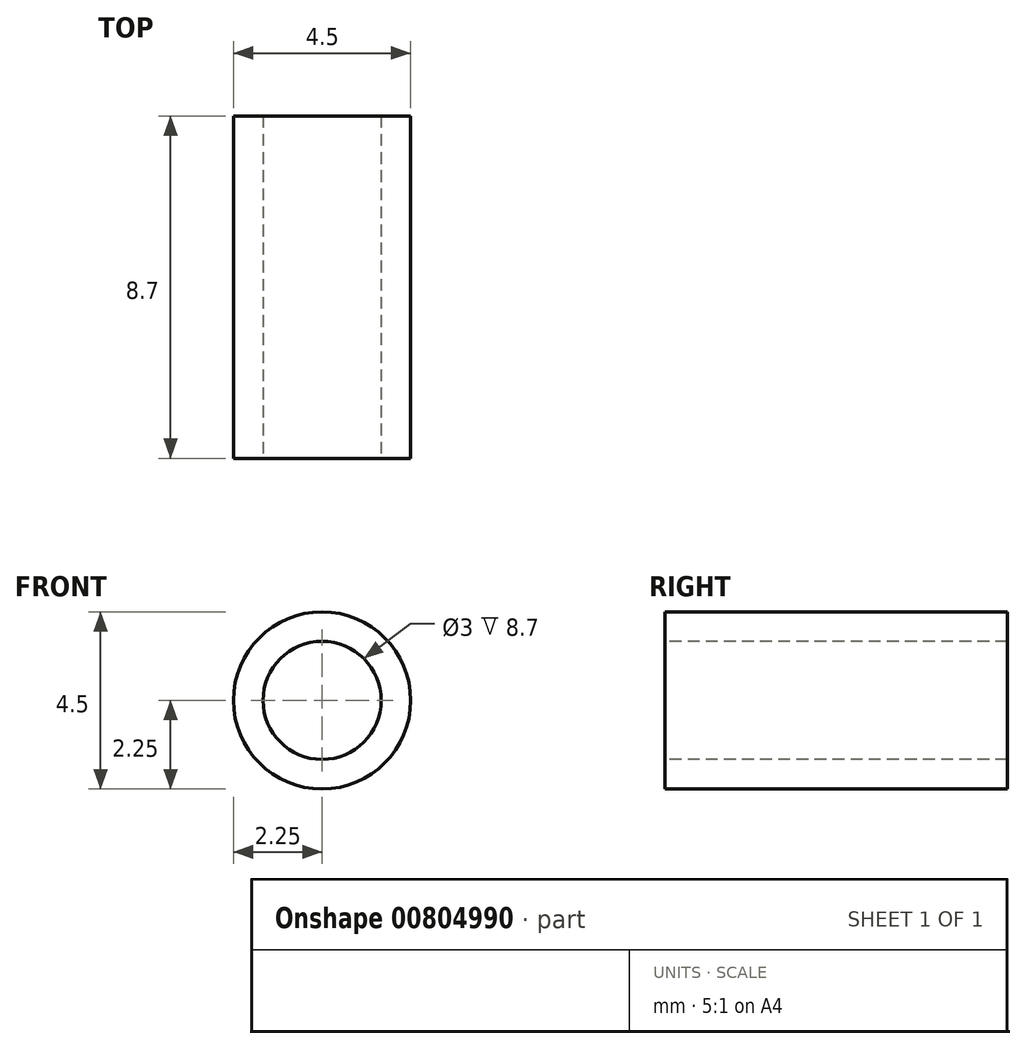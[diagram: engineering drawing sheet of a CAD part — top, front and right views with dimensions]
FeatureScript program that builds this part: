
annotation { "Feature Type Name" : "Feature", "Feature Type Description" : "" }
export const myFeature = defineFeature(function(context is Context, id is Id, definition is map)
    precondition{}
    {
        {
            var Q0;
            Q0=qCreatedBy(makeId("Right.planeOp"),FACE);
            var sketch = newSketch(context, id + "F0", { "sketchPlane" : qUnion([Q0])});
            skLineSegment(sketch, "E0.bottom", {"start": v(4.35, 1.5) * mm, "end": v(-4.35, 1.5) * mm});
            skLineSegment(sketch, "E0.top", {"start": v(4.35, 2.25) * mm, "end": v(-4.35, 2.25) * mm});
            skLineSegment(sketch, "E0.left", {"start": v(4.35, 1.5) * mm, "end": v(4.35, 2.25) * mm});
            skLineSegment(sketch, "E0.right", {"start": v(-4.35, 1.5) * mm, "end": v(-4.35, 2.25) * mm});
            skPoint(sketch, "E0.middle", {"position": v(0, 1.87) * mm});
            skLineSegment(sketch, "E1", {"start": v(-3.4, 0) * mm, "end": v(3.9, 0) * mm, "construction": true});
            skSolve(sketch);
        }
        {
            var Q0;
            Q0=makeQuery(id+"F0.imprint","IMPRINT",FACE,{"disambiguationData":[TD([[makeQuery(id+"F0.imprint","IMPRINT",EDGE,{"derivedFrom":sQuery(id+"F0.wireOp",EDGE,"E0.bottom")}),-1.0]])]});
            var Q1;
            Q1=sQuery(id+"F0.wireOp",EDGE,"E1");
            revolve(context, id + "F1", {"entities" : qUnion([Q0]), "axis" : qUnion([Q1]), "revolveType" : RevolveType.FULL});
        }
    });
